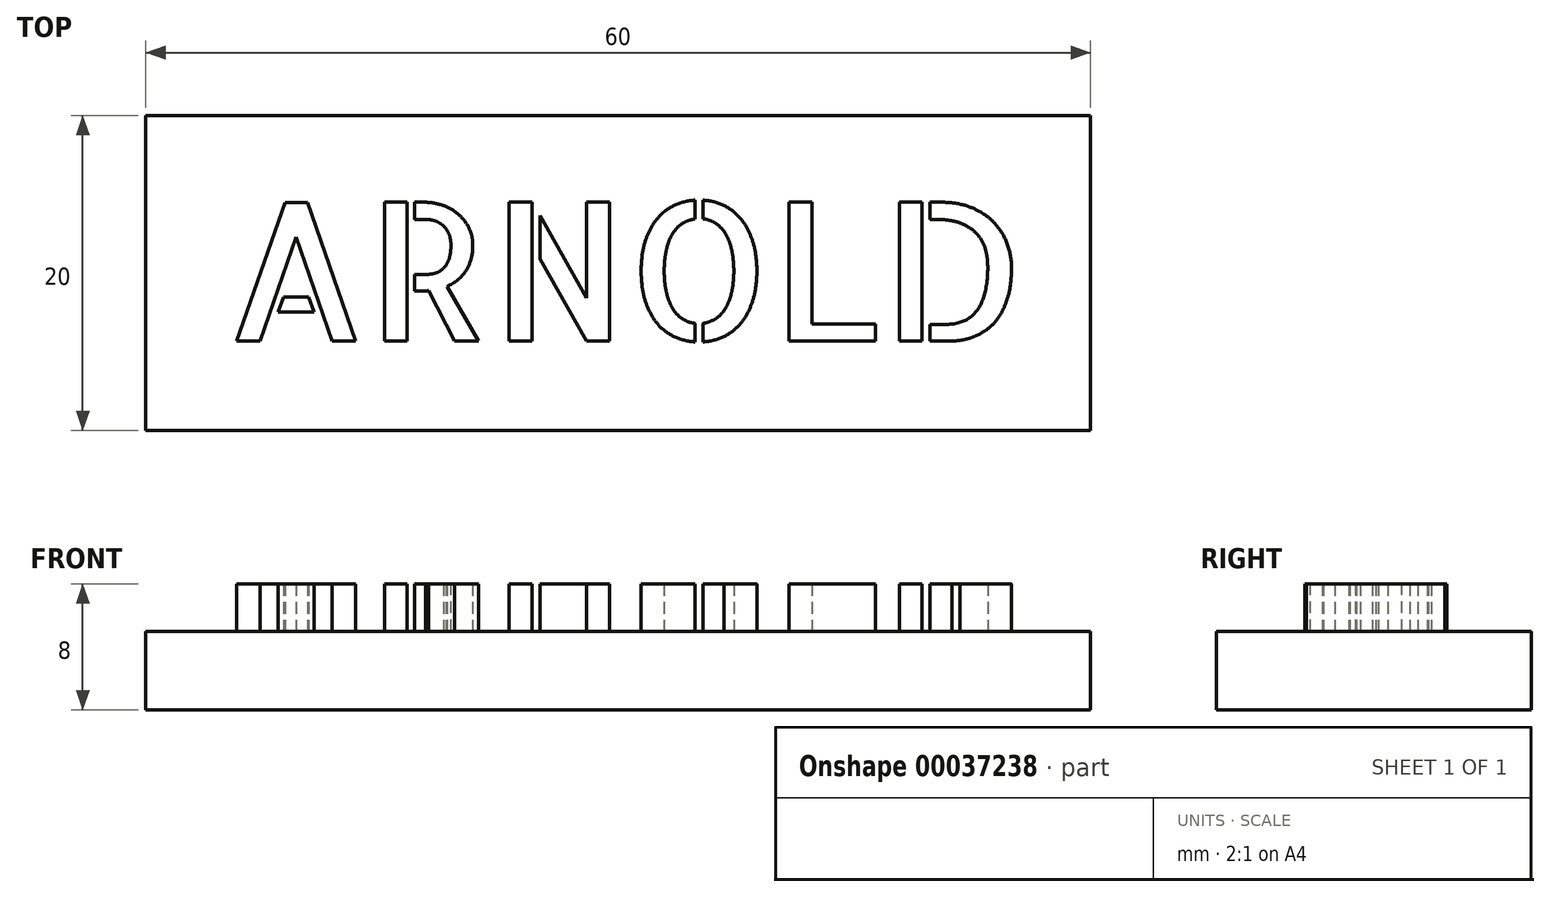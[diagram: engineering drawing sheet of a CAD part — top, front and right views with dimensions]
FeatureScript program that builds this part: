
annotation { "Feature Type Name" : "Feature", "Feature Type Description" : "" }
export const myFeature = defineFeature(function(context is Context, id is Id, definition is map)
    precondition{}
    {
        {
            var Q0;
            Q0=qCreatedBy(makeId("Top.planeOp"),FACE);
            var sketch = newSketch(context, id + "F0", { "sketchPlane" : qUnion([Q0])});
            skLineSegment(sketch, "E0.rect.bottom", {"start": v(-30, 10) * mm, "end": v(30, 10) * mm});
            skLineSegment(sketch, "E0.rect.top", {"start": v(-30, -10) * mm, "end": v(30, -10) * mm});
            skLineSegment(sketch, "E0.rect.left", {"start": v(-30, 10) * mm, "end": v(-30, -10) * mm});
            skLineSegment(sketch, "E0.rect.right", {"start": v(30, 10) * mm, "end": v(30, -10) * mm});
            skPoint(sketch, "E0.rect.middle", {"position": v(0, 0) * mm});
            skSolve(sketch);
        }
        {
            var Q0;
            Q0 = qSketchRegion(id + "F0", true);
            extrude(context, id + "F1", {"entities" : qUnion([Q0]), "depth" : 5 * mm});
        }
        {
            var Q0;
            Q0=makeQuery(id+"F1.opExtrude","CAP_FACE",FACE,{"disambiguationData":[OSD([sQuery(id+"F0.wireOp",EDGE,"E0.rect.bottom"),sQuery(id+"F0.wireOp",EDGE,"E0.rect.top"),sQuery(id+"F0.wireOp",EDGE,"E0.rect.left"),sQuery(id+"F0.wireOp",EDGE,"E0.rect.right")])],"isStart":false});
            var sketch = newSketch(context, id + "F2", { "sketchPlane" : qUnion([Q0])});
            skText(sketch, "E1", { "text": "ARNOLD", "fontName": "AllertaStencil-Regular.ttf"});
            const initialGuessF2  = {"E1": [-0.025, -0.00432, 1, 0, 0.00882]};
            skSetInitialGuess(sketch, initialGuessF2);
            skSolve(sketch);
        }
        {
            var Q0;
            Q0 = qSketchRegion(id + "F2", true);
            extrude(context, id + "F3", {"entities" : qUnion([Q0]), "operationType" : NewBodyOperationType.ADD, "depth" : 3 * mm});
        }
    });
